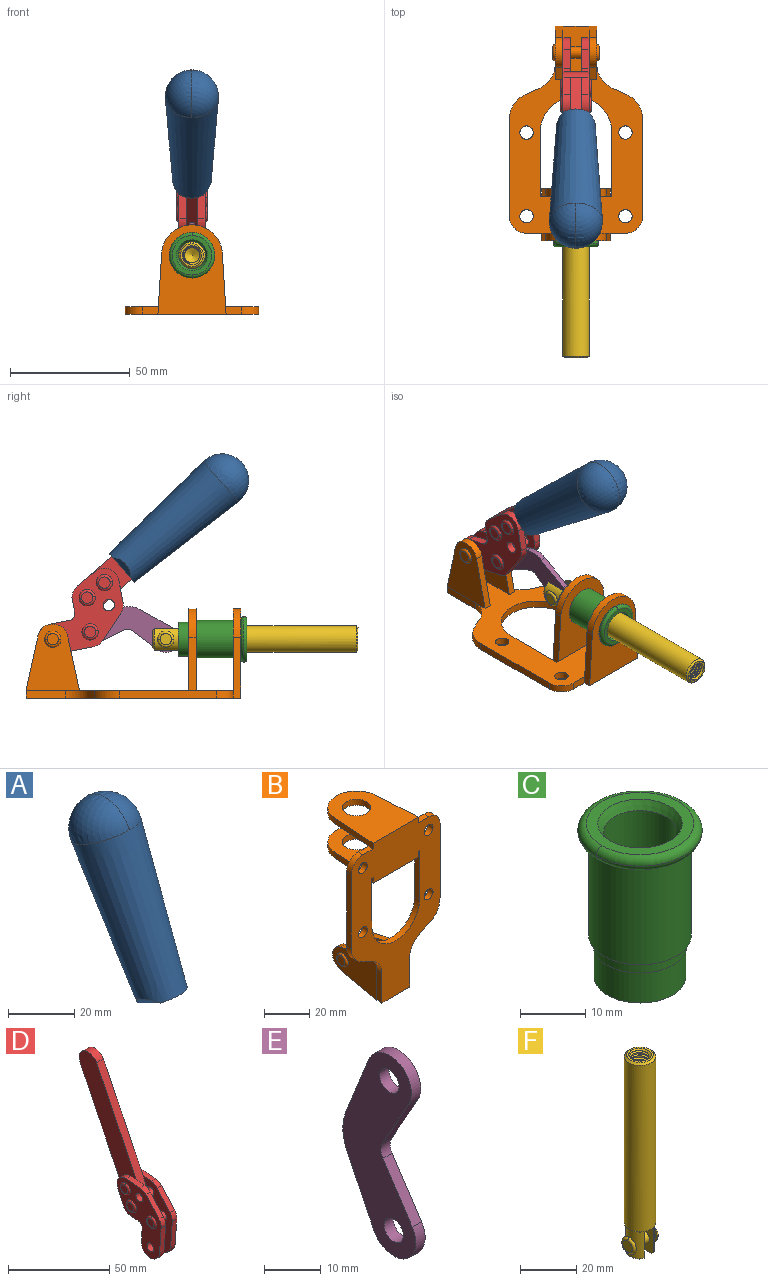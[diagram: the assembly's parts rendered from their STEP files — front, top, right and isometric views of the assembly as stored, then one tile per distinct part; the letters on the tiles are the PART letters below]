
ASSEMBLY  parts=6 mates=6
PART A: 11 faces, bbox 22.3x42.6x64.5 mm
  f0: sphere r=11.13mm, area 411.4mm2, adj f1,f8
  f1: cone r=11.11mm half-angle=3.3deg, axis (0,0.44,0.9), area 3251.8mm2, adj f0,f7,f8,f9,f10
  f2: cylinder r=6.16mm len=11.7mm, axis (1,0,0), area 89.5mm2, adj f3,f4,f5,f6
  f3: plane 60.23x36.75mm, normal (-1,0,0), area 763.6mm2, adj f2,f4,f6,f10
  f4: plane 51.37x25.05mm, normal (0,0.9,-0.44), area 264.2mm2, adj f2,f3,f5,f10
  f5: plane 60.23x36.75mm, normal (1,0,0), area 763.6mm2, adj f2,f4,f6,f10
  f6: plane 51.37x25.05mm, normal (0,-0.9,0.44), area 264.2mm2, adj f2,f3,f5,f10
  f7: plane 9.95x5.95mm, normal (0.71,-0.31,-0.64), area 25.8mm2, adj f1,f10
  f8: sphere r=11.13mm, area 411.4mm2, adj f0,f1
  f9: plane 9.95x5.95mm, normal (-0.71,-0.31,-0.64), area 25.8mm2, adj f1,f10
  f10: plane 14.27x11.38mm, normal (0,-0.44,-0.9), area 106.7mm2, adj f1,f3,f4,f5,f6,f7,f9
PART B: 55 faces, bbox 55.7x37.4x89.8 mm
  f0: torus R=2.41mm, axis (-1,0,0), area 15mm2, adj f11,f15,f25
  f1: torus R=2.41mm, axis (-1,0,0), area 15mm2, adj f10,f12,f22
  f2: cylinder r=2.78mm len=5.56mm, axis (0,-1,0), area 54.2mm2, adj f30,f54
  f3: cylinder r=14.99mm len=29.97mm, axis (0,-1,0), area 145.9mm2, adj f30,f49,f53,f54
  f4: cylinder r=2.78mm len=5.56mm, axis (0,-1,0), area 54.2mm2, adj f30,f54
  f5: cylinder r=2.78mm len=5.56mm, axis (0,-1,0), area 54.2mm2, adj f30,f54
  f6: cylinder r=2.78mm len=5.56mm, axis (0,-1,0), area 54.2mm2, adj f30,f54
  f7: cylinder r=6.35mm len=12.7mm, axis (0,0,1), area 123.6mm2, adj f27,f51
  f8: cylinder r=6.35mm len=12.7mm, axis (0,0,-1), area 124.7mm2, adj f21,f35
  f9: cylinder r=2.41mm len=11.18mm, axis (-1,0,0), area 169.4mm2, adj f16,f19
  f10: plane 4.83x4.83mm, normal (1,0,0), area 18.3mm2, adj f1,f12
  f11: plane 4.83x4.83mm, normal (-1,0,0), area 18.3mm2, adj f0,f15
  f12: torus R=2.41mm, axis (-1,0,0), area 15mm2, adj f1,f10,f22
  f13: cylinder r=6.35mm len=12.41mm, axis (1,0,0), area 53.4mm2, adj f18,f19,f22,f23
  f14: cylinder r=6.35mm len=12.41mm, axis (-1,0,0), area 53.4mm2, adj f16,f17,f24,f25
  f15: torus R=2.41mm, axis (-1,0,0), area 15mm2, adj f0,f11,f25
  f16: plane 27.86x22.35mm, normal (1,0,0), area 425.4mm2, adj f9,f14,f17,f24,f30
  f17: plane 22.86x4.97mm, normal (0,0.21,0.98), area 72.5mm2, adj f14,f16,f25,f30
  f18: plane 22.86x4.97mm, normal (0,0.21,0.98), area 72.5mm2, adj f13,f19,f22,f30
  f19: plane 27.86x22.35mm, normal (-1,0,0), area 425.4mm2, adj f9,f13,f18,f23,f30
  f20: cylinder r=12.7mm len=25.35mm, axis (0,0,-1), area 119.8mm2, adj f21,f34,f35,f36
  f21: plane 34.21x28.07mm, normal (0,0,-1), area 702.4mm2, adj f8,f20,f30,f34,f36
  f22: plane 27.96x22.45mm, normal (1,0,0), area 407.2mm2, adj f1,f12,f13,f18,f23,f30,f42,f43
  f23: plane 22.86x4.97mm, normal (0,0.21,-0.98), area 72.5mm2, adj f13,f19,f22,f44
  f24: plane 22.86x4.97mm, normal (0,0.21,-0.98), area 72.5mm2, adj f14,f16,f25,f44
  f25: plane 27.86x22.35mm, normal (-1,0,0), area 407.1mm2, adj f0,f14,f15,f17,f24,f30,f45,f46
  f26: plane 3.1x0.95mm, normal (0,0,-1), area 2.7mm2, adj f30,f49,f50,f54
  f27: plane 34.21x28.07mm, normal (0,0,1), area 702.4mm2, adj f7,f28,f30,f50,f52
  f28: cylinder r=12.7mm len=25.35mm, axis (0,0,1), area 118.8mm2, adj f27,f50,f51,f52
  f29: plane 3.1x0.95mm, normal (0,0,-1), area 2.7mm2, adj f30,f52,f53,f54
  f30: plane 86.54x55.63mm, normal (0,1,0), area 2362.9mm2, adj f2,f3,f4,f5,f6,f16,f17,f18
  f31: plane 40.56x3.1mm, normal (-1,0,0), area 125.7mm2, adj f30,f32,f48,f54
  f32: cylinder r=7.11mm len=7.11mm, axis (0,-1,0), area 34.6mm2, adj f30,f31,f33,f54
  f33: plane 6.67x3.1mm, normal (0,0,1), area 20.4mm2, adj f30,f32,f34,f54
  f34: plane 25.39x3.13mm, normal (-1,0.06,0), area 79.5mm2, adj f20,f21,f33,f35,f54
  f35: plane 37.31x28.45mm, normal (0,0,1), area 789.9mm2, adj f8,f20,f34,f36,f54
  f36: plane 25.39x3.13mm, normal (1,0.06,0), area 79.5mm2, adj f20,f21,f35,f37,f54
  f37: plane 6.67x3.1mm, normal (0,0,1), area 20.4mm2, adj f30,f36,f38,f54
  f38: cylinder r=7.11mm len=7.11mm, axis (0,-1,0), area 34.6mm2, adj f30,f37,f39,f54
  f39: plane 40.56x3.1mm, normal (1,0,0), area 125.7mm2, adj f30,f38,f40,f54
  f40: cylinder r=11.18mm len=10.16mm, axis (0,-1,0), area 39.5mm2, adj f30,f39,f41,f54
  f41: plane 6.09x3.1mm, normal (0.42,0,-0.91), area 20.8mm2, adj f30,f40,f42,f54
  f42: cylinder r=11.18mm len=9.41mm, axis (0,-1,0), area 37.2mm2, adj f22,f30,f41,f43,f54
  f43: plane 16.5x3.1mm, normal (1,0,0), area 51.1mm2, adj f22,f42,f44,f54
  f44: plane 17.37x3.1mm, normal (0,0,-1), area 53.8mm2, adj f23,f24,f30,f43,f45,f54
  f45: plane 16.5x3.1mm, normal (-1,0,0), area 51.1mm2, adj f25,f44,f46,f54
  f46: cylinder r=11.18mm len=9.41mm, axis (0,-1,0), area 37.2mm2, adj f25,f30,f45,f47,f54
  f47: plane 6.09x3.1mm, normal (-0.42,0,-0.91), area 20.8mm2, adj f30,f46,f48,f54
  f48: cylinder r=11.18mm len=10.16mm, axis (0,-1,0), area 39.5mm2, adj f30,f31,f47,f54
  f49: plane 26.54x3.1mm, normal (-1,0,0), area 82.3mm2, adj f3,f26,f30,f54
  f50: plane 25.39x3.1mm, normal (1,0.06,0), area 78.8mm2, adj f26,f27,f28,f51,f54
  f51: plane 37.31x28.45mm, normal (0,0,-1), area 789.9mm2, adj f7,f28,f50,f52,f54
  f52: plane 25.39x3.1mm, normal (-1,0.06,0), area 78.8mm2, adj f27,f28,f29,f51,f54
  f53: plane 26.54x3.1mm, normal (1,0,0), area 82.3mm2, adj f3,f29,f30,f54
  f54: plane 89.66x55.63mm, normal (0,-1,0), area 2678.5mm2, adj f2,f3,f4,f5,f6,f26,f29,f31
PART C: 15 faces, bbox 20.6x20.6x28.7 mm
  f0: torus R=8.26mm, axis (0,0,1), area 56.8mm2, adj f1,f10,f12
  f1: torus R=8.26mm, axis (0,0,1), area 56.8mm2, adj f0,f6,f13
  f2: cylinder r=5.59mm len=25.91mm, axis (0,0,1), area 909.6mm2, adj f3,f4
  f3: cone r=6.86mm half-angle=45deg, axis (0,0,-1), area 70.2mm2, adj f2,f14
  f4: cone r=6.47mm half-angle=30deg, axis (0,0,1), area 66.7mm2, adj f2,f13
  f5: cylinder r=7.04mm len=14.07mm, axis (0,0,1), area 252.6mm2, adj f11,f14
  f6: torus R=8.26mm, axis (0,0,1), area 56.8mm2, adj f1,f12,f13
  f7: cylinder r=7.16mm len=14.33mm, axis (0,0,1), area 91.5mm2, adj f9,f11
  f8: cylinder r=7.86mm len=18.42mm, axis (0,0,1), area 909.6mm2, adj f9,f10
  f9: plane 15.72x15.72mm, normal (0,0,-1), area 33mm2, adj f7,f8
  f10: plane 16.51x16.51mm, normal (0,0,-1), area 19.9mm2, adj f0,f8,f12
  f11: plane 14.33x14.33mm, normal (0,0,-1), area 5.7mm2, adj f5,f7
  f12: torus R=8.26mm, axis (0,0,1), area 56.8mm2, adj f0,f6,f10
  f13: plane 16.51x16.51mm, normal (0,0,1), area 82.7mm2, adj f1,f4,f6
  f14: plane 14.07x14.07mm, normal (0,0,-1), area 7.8mm2, adj f3,f5
PART D: 59 faces, bbox 12.9x60.2x99.6 mm
  f0: torus R=2.39mm, axis (-1,0,0), area 14.9mm2, adj f20,f43,f51
  f1: torus R=2.39mm, axis (-1,0,0), area 14.9mm2, adj f19,f42,f51
  f2: torus R=2.39mm, axis (-1,0,0), area 14.9mm2, adj f18,f35,f51
  f3: torus R=2.39mm, axis (-1,0,0), area 14.9mm2, adj f14,f17,f23
  f4: torus R=2.39mm, axis (-1,0,0), area 14.9mm2, adj f13,f16,f23
  f5: torus R=2.39mm, axis (-1,0,0), area 14.9mm2, adj f12,f15,f23
  f6: cylinder r=2.39mm len=4.78mm, axis (1,0,0), area 46.5mm2, adj f48,f50,f51
  f7: cylinder r=2.39mm len=4.78mm, axis (1,0,0), area 46.5mm2, adj f50,f51
  f8: cylinder r=6.35mm len=12.68mm, axis (1,0,0), area 61.8mm2, adj f38,f39,f50,f51
  f9: cylinder r=2.39mm len=4.78mm, axis (-1,0,0), area 70.5mm2, adj f46,f50
  f10: cylinder r=2.39mm len=4.78mm, axis (-1,0,0), area 46.5mm2, adj f23,f45,f46
  f11: cylinder r=2.39mm len=4.78mm, axis (-1,0,0), area 46.5mm2, adj f23,f46
  f12: plane 4.78x4.78mm, normal (1,0,0), area 17.9mm2, adj f5,f15
  f13: plane 4.78x4.78mm, normal (1,0,0), area 17.9mm2, adj f4,f16
  f14: plane 4.78x4.78mm, normal (1,0,0), area 17.9mm2, adj f3,f17
  f15: torus R=2.39mm, axis (-1,0,0), area 14.9mm2, adj f5,f12,f23
  f16: torus R=2.39mm, axis (-1,0,0), area 14.9mm2, adj f4,f13,f23
  f17: torus R=2.39mm, axis (-1,0,0), area 14.9mm2, adj f3,f14,f23
  f18: plane 4.78x4.78mm, normal (-1,0,0), area 17.9mm2, adj f2,f35
  f19: plane 4.78x4.78mm, normal (-1,0,0), area 17.9mm2, adj f1,f42
  f20: plane 4.78x4.78mm, normal (-1,0,0), area 17.9mm2, adj f0,f43
  f21: plane 2.26x0.2mm, normal (1,0,0), area 0.2mm2, adj f31,f44
  f22: plane 2.26x0.2mm, normal (-1,0,0), area 0.2mm2, adj f41,f44
  f23: plane 39.37x30.77mm, normal (1,0,0), area 565.5mm2, adj f3,f4,f5,f10,f11,f15,f16,f17
  f24: cylinder r=6.1mm len=4.15mm, axis (-1,0,0), area 14.7mm2, adj f23,f25,f32,f46
  f25: plane 10.25x9.01mm, normal (0,-0.75,0.66), area 42.3mm2, adj f23,f24,f26,f46
  f26: cylinder r=6.35mm len=4.64mm, axis (-1,0,0), area 15.6mm2, adj f23,f25,f27,f46
  f27: plane 15.84x3.1mm, normal (0,-1,-0.07), area 49.2mm2, adj f23,f26,f28,f46
  f28: cylinder r=6.35mm len=12.68mm, axis (-1,0,0), area 61.8mm2, adj f23,f27,f29,f46
  f29: plane 8.11x3.1mm, normal (0,1,0.07), area 25.2mm2, adj f23,f28,f30,f46
  f30: cylinder r=3.05mm len=3.25mm, axis (-1,0,0), area 14.8mm2, adj f23,f29,f31,f46
  f31: plane 5.99x3.1mm, normal (0,0.07,-1), area 18.6mm2, adj f21,f23,f30,f44,f46
  f32: plane 9.5x3.1mm, normal (0,-0.07,1), area 29.5mm2, adj f23,f24,f33,f46,f47
  f33: cylinder r=6.1mm len=8.63mm, axis (-1,0,0), area 39.1mm2, adj f23,f32,f34,f47
  f34: plane 8.65x3.96mm, normal (0,0.91,-0.42), area 29.5mm2, adj f23,f33,f44,f47
  f35: torus R=2.39mm, axis (-1,0,0), area 14.9mm2, adj f2,f18,f51
  f36: plane 10.25x9.01mm, normal (0,-0.75,0.66), area 42.3mm2, adj f37,f49,f50,f51
  f37: cylinder r=6.35mm len=4.64mm, axis (1,0,0), area 15.6mm2, adj f36,f38,f50,f51
  f38: plane 15.84x3.1mm, normal (0,-1,-0.07), area 49.2mm2, adj f8,f37,f50,f51
  f39: plane 8.11x3.1mm, normal (0,1,0.07), area 25.2mm2, adj f8,f40,f50,f51
  f40: cylinder r=3.05mm len=3.25mm, axis (1,0,0), area 14.8mm2, adj f39,f41,f50,f51
  f41: plane 5.99x3.1mm, normal (0,0.07,-1), area 18.6mm2, adj f22,f40,f44,f50,f51
  f42: torus R=2.39mm, axis (-1,0,0), area 14.9mm2, adj f1,f19,f51
  f43: torus R=2.39mm, axis (-1,0,0), area 14.9mm2, adj f0,f20,f51
  f44: cylinder r=6.35mm len=12.12mm, axis (-1,0,0), area 128.9mm2, adj f21,f22,f23,f31,f34,f41,f46,f47
  f45: plane 2.65x1.35mm, normal (1,0,0), area 1mm2, adj f10,f55
  f46: plane 39.08x20.42mm, normal (-1,0,0), area 412.5mm2, adj f9,f10,f11,f24,f25,f26,f27,f28
  f47: plane 77.62x39.82mm, normal (1,0,0), area 850mm2, adj f32,f33,f34,f44,f53,f54,f55
  f48: plane 2.65x1.35mm, normal (-1,0,0), area 1mm2, adj f6,f55
  f49: cylinder r=6.1mm len=4.15mm, axis (1,0,0), area 14.7mm2, adj f36,f50,f51,f56
  f50: plane 39.08x20.42mm, normal (1,0,0), area 412.5mm2, adj f6,f7,f8,f9,f36,f37,f38,f39
  f51: plane 39.37x30.77mm, normal (-1,0,0), area 565.5mm2, adj f0,f1,f2,f6,f7,f8,f35,f36
  f52: plane 8.65x3.96mm, normal (0,0.91,-0.42), area 29.5mm2, adj f44,f51,f57,f58
  f53: plane 68.49x33.4mm, normal (0,0.9,-0.44), area 358.1mm2, adj f44,f47,f54,f58
  f54: cylinder r=6.35mm len=12.06mm, axis (1,0,0), area 93.7mm2, adj f47,f53,f55,f58
  f55: plane 68.49x33.4mm, normal (0,-0.9,0.44), area 358.1mm2, adj f44,f45,f46,f47,f48,f50,f54,f58
  f56: plane 9.5x3.1mm, normal (0,-0.07,1), area 29.5mm2, adj f49,f50,f51,f57,f58
  f57: cylinder r=6.1mm len=8.63mm, axis (1,0,0), area 39.1mm2, adj f51,f52,f56,f58
  f58: plane 77.62x39.82mm, normal (-1,0,0), area 850mm2, adj f44,f52,f53,f54,f55,f56,f57
PART E: 12 faces, bbox 2.3x18.2x42.8 mm
  f0: cylinder r=2.4mm len=4.8mm, axis (1,0,0), area 34.9mm2, adj f4,f11
  f1: cylinder r=10.41mm len=8.47mm, axis (1,0,0), area 20.2mm2, adj f4,f9,f10,f11
  f2: cylinder r=3.05mm len=3.16mm, axis (1,0,0), area 7.7mm2, adj f4,f6,f7,f11
  f3: cylinder r=2.4mm len=4.8mm, axis (1,0,0), area 34.9mm2, adj f4,f11
  f4: plane 42.81x18.23mm, normal (-1,0,0), area 414.1mm2, adj f0,f1,f2,f3,f5,f6,f7,f8
  f5: cylinder r=5.54mm len=10.67mm, axis (1,0,0), area 41.8mm2, adj f4,f6,f10,f11
  f6: plane 11.66x6.53mm, normal (0,-0.87,-0.49), area 30.9mm2, adj f2,f4,f5,f11
  f7: plane 11.17x7.33mm, normal (0,-0.84,0.55), area 30.9mm2, adj f2,f4,f8,f11
  f8: cylinder r=5.54mm len=10.51mm, axis (1,0,0), area 41.8mm2, adj f4,f7,f9,f11
  f9: plane 13.67x6.67mm, normal (0,0.9,-0.44), area 35.1mm2, adj f1,f4,f8,f11
  f10: plane 14.1x5.7mm, normal (0,0.93,0.37), area 35.1mm2, adj f1,f4,f5,f11
  f11: plane 42.81x18.23mm, normal (1,0,0), area 414.1mm2, adj f0,f1,f2,f3,f5,f6,f7,f8
PART F: 48 faces, bbox 12.6x11.1x86.1 mm
  f0: torus R=2.41mm, axis (-1,0,0), area 15mm2, adj f30,f32,f34
  f1: torus R=2.41mm, axis (-1,0,0), area 15mm2, adj f29,f31,f33
  f2: cylinder r=5.54mm len=72.39mm, axis (0,0,1), area 2518.5mm2, adj f3,f4,f42,f43
  f3: cone r=5.54mm half-angle=45deg, axis (0,0,1), area 7.6mm2, adj f2,f5,f41
  f4: cone r=5.54mm half-angle=45deg, axis (0,0,-1), area 34.9mm2, adj f2,f39
  f5: cylinder r=5.08mm len=11.48mm, axis (0,0,1), area 108.3mm2, adj f3,f7,f8,f41
  f6: cylinder r=2.41mm len=4.83mm, axis (-1,0,0), area 71.2mm2, adj f40,f41
  f7: cylinder r=2.41mm len=4.83mm, axis (-1,0,0), area 7.6mm2, adj f5,f34
  f8: cone r=5.08mm half-angle=45deg, axis (0,0,1), area 10.6mm2, adj f5,f37,f41
  f9: cone r=3.98mm half-angle=45deg, axis (0,0,1), area 17.6mm2, adj f27,f39,f45,f46,f47
  f10: cylinder r=2.41mm len=4.83mm, axis (-1,0,0), area 7.6mm2, adj f33,f38
  f11: cylinder r=3.2mm len=6.4mm, axis (0,0,1), area 78.4mm2, adj f12,f28,f44,f45,f47
  f12: cylinder r=3.2mm len=6.4mm, axis (0,0,1), area 10.5mm2, adj f11,f13,f45,f47
  f13: cylinder r=3.2mm len=6.4mm, axis (0,0,1), area 10.5mm2, adj f12,f14,f45,f47
  f14: cylinder r=3.2mm len=6.4mm, axis (0,0,1), area 10.5mm2, adj f13,f15,f45,f47
  f15: cylinder r=3.2mm len=6.4mm, axis (0,0,1), area 10.5mm2, adj f14,f16,f45,f47
  f16: cylinder r=3.2mm len=6.4mm, axis (0,0,1), area 10.5mm2, adj f15,f17,f45,f47
  f17: cylinder r=3.2mm len=6.4mm, axis (0,0,1), area 10.5mm2, adj f16,f18,f45,f47
  f18: cylinder r=3.2mm len=6.4mm, axis (0,0,1), area 10.5mm2, adj f17,f19,f45,f47
  f19: cylinder r=3.2mm len=6.4mm, axis (0,0,1), area 10.5mm2, adj f18,f20,f45,f47
  f20: cylinder r=3.2mm len=6.4mm, axis (0,0,1), area 10.5mm2, adj f19,f21,f45,f47
  f21: cylinder r=3.2mm len=6.4mm, axis (0,0,1), area 10.5mm2, adj f20,f22,f45,f47
  f22: cylinder r=3.2mm len=6.4mm, axis (0,0,1), area 10.5mm2, adj f21,f23,f45,f47
  f23: cylinder r=3.2mm len=6.4mm, axis (0,0,1), area 10.5mm2, adj f22,f24,f45,f47
  f24: cylinder r=3.2mm len=6.4mm, axis (0,0,1), area 10.5mm2, adj f23,f25,f45,f47
  f25: cylinder r=3.2mm len=6.4mm, axis (0,0,1), area 10.5mm2, adj f24,f26,f45,f47
  f26: cylinder r=3.2mm len=6.4mm, axis (0,0,1), area 10.5mm2, adj f25,f27,f45,f47
  f27: cylinder r=3.2mm len=6.4mm, axis (0,0,1), area 7.4mm2, adj f9,f26,f45,f47
  f28: cone r=3.2mm half-angle=60deg, axis (0,0,1), area 37.2mm2, adj f11
  f29: plane 4.83x4.83mm, normal (-1,0,0), area 18.3mm2, adj f1,f31
  f30: plane 4.83x4.83mm, normal (1,0,0), area 18.3mm2, adj f0,f32
  f31: torus R=2.41mm, axis (-1,0,0), area 15mm2, adj f1,f29,f33
  f32: torus R=2.41mm, axis (-1,0,0), area 15mm2, adj f0,f30,f34
  f33: plane 6.83x6.83mm, normal (1,0,0), area 18.3mm2, adj f1,f10,f31
  f34: plane 6.83x6.83mm, normal (-1,0,0), area 18.3mm2, adj f0,f7,f32
  f35: cone r=5.08mm half-angle=45deg, axis (0,0,1), area 10.6mm2, adj f36,f38,f40
  f36: plane 7.25x1.97mm, normal (0,0,-1), area 10mm2, adj f35,f40
  f37: plane 7.25x1.97mm, normal (0,0,-1), area 10mm2, adj f8,f41
  f38: cylinder r=5.08mm len=11.48mm, axis (0,0,1), area 108.3mm2, adj f10,f35,f40,f42
  f39: plane 9.55x9.55mm, normal (0,0,1), area 22mm2, adj f4,f9
  f40: plane 12.76x10.09mm, normal (1,0,0), area 95.7mm2, adj f6,f35,f36,f38,f42,f43
  f41: plane 12.76x10.09mm, normal (-1,0,0), area 95.7mm2, adj f3,f5,f6,f8,f37,f43
  f42: cone r=5.54mm half-angle=45deg, axis (0,0,1), area 7.6mm2, adj f2,f38,f40
  f43: plane 11.07x4.7mm, normal (0,0,-1), area 50.4mm2, adj f2,f40,f41
  f44: plane 0.89x0.62mm, normal (-1,0,0), area 0.3mm2, adj f11,f45,f46,f47
  f45: bspline ~24.8x7.63mm, area 266.6mm2, adj f9,f11,f12,f13,f14,f15,f16,f17
  f46: bspline ~24.87x7.63mm, area 73.6mm2, adj f9,f44,f45,f47
  f47: bspline ~24.98x7.63mm, area 272.5mm2, adj f9,f11,f12,f13,f14,f15,f16,f17
PLACE A rot(axis=(1,0,0),75deg) t=(32.98,29.31,-9.51)mm
PLACE B rot(axis=(1,0,0),90deg) t=(33.02,34.58,-18.66)mm
PLACE C rot(axis=(0.58,-0.58,0.58),120deg) t=(57.63,34.58,5.96)mm
PLACE D rot(axis=(1,0,0),75deg) t=(33.02,29.31,-9.51)mm
PLACE E rot(axis=(0,0.69,0.73),180deg) t=(33.02,37.14,-16.52)mm
PLACE F rot(axis=(1,0,0),90deg) t=(33.02,34.96,-18.66)mm
MATE slider F.f2 <-> C.f2  axis (0,-1,0) through (33.02,-23.82,5.96)mm
MATE revolute B.f0 <-> D.f7  axis (-1,0,0) through (33.02,66.68,5.96)mm
MATE revolute E.f3 <-> F.f6  axis (-1,0,0) through (33.02,19.49,5.96)mm
MATE fastened C.f0 <-> B.f7  axis (0,1,0) through (33.02,-11.81,5.96)mm
MATE fastened A.f2 <-> D.f54  axis (1,0,0) through (30.67,-5.21,73.28)mm
MATE revolute E.f5 <-> D.f4  axis (-1,0,0) through (33.02,51.09,8.99)mm
